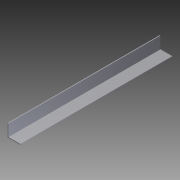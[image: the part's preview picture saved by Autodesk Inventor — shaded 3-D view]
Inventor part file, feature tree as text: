
AUTODESK INVENTOR PART (.ipt)
format: ipt  version: 2012 (Build 160160000, 160)  size: 73,728 bytes
history: native  units: in
note: dims shown in document units (in); Inventor stores cm internally (conversion verified against a paired STEP export)
features: extrude x1, sketch x1
ambient origin geometry x8: Origin, YZ Plane, XZ Plane, XY Plane, X Axis, Y Axis, Z Axis, Center Point
bodies: Solid1 (feature_tree)
feature tree (2):
  extrude  "Extrusion1"  Depth=1.0in
  sketch  "Sketch1"  dims[d0=1.0in d1=1.0in d2=0.0625in d3=0.0625in d4=12.0in d5=0.0in]
